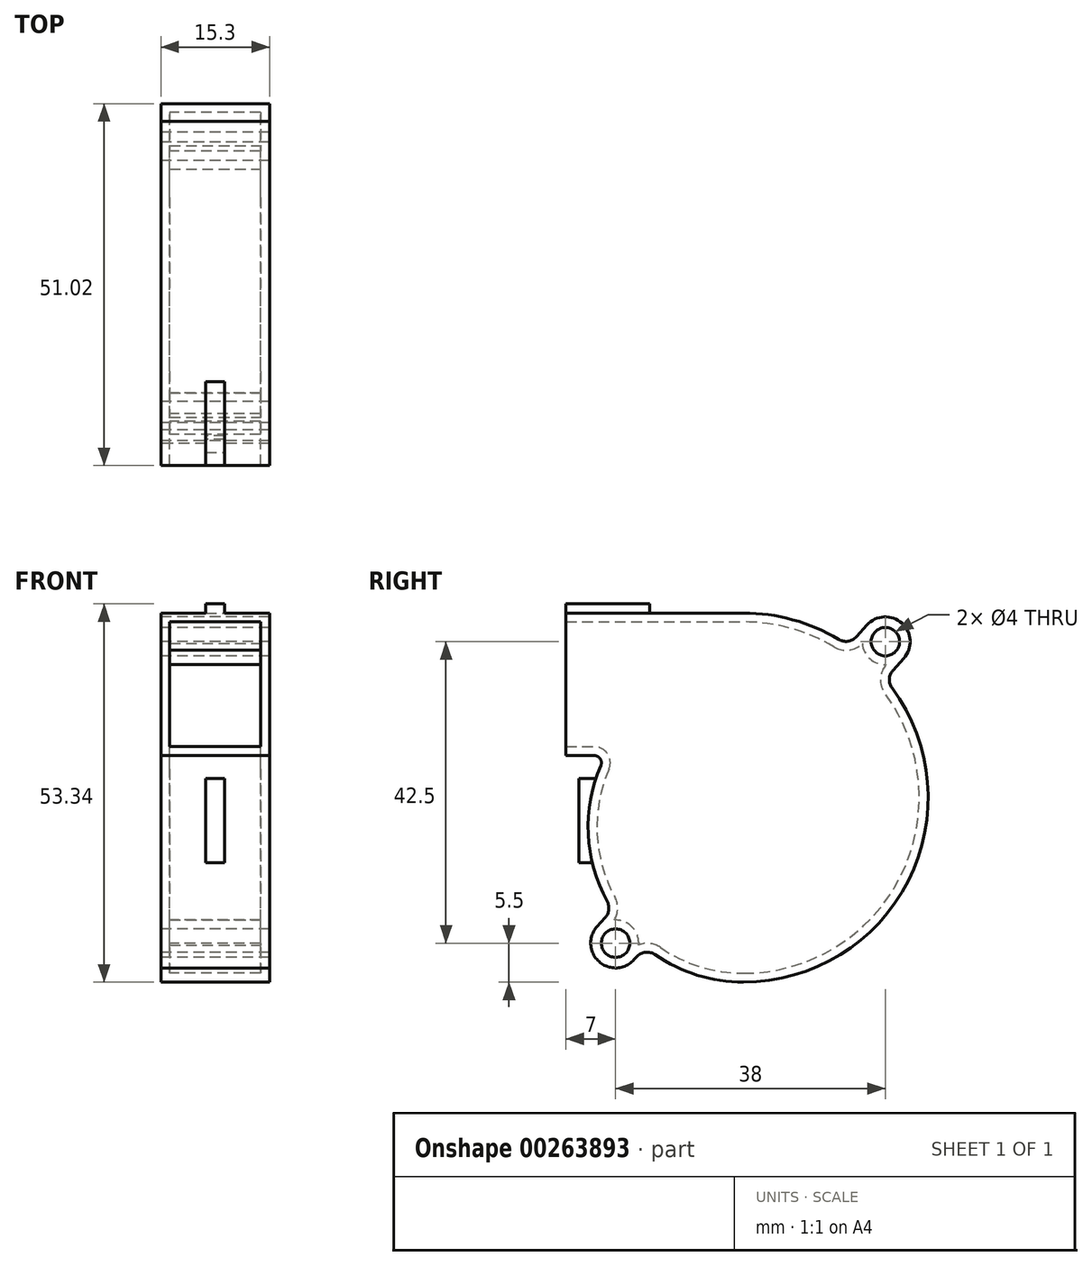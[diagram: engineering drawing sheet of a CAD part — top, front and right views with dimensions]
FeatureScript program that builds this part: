
annotation { "Feature Type Name" : "Feature", "Feature Type Description" : "" }
export const myFeature = defineFeature(function(context is Context, id is Id, definition is map)
    precondition{}
    {
        {
            var Q0;
            Q0=qCreatedBy(makeId("Right.planeOp"),FACE);
            var sketch = newSketch(context, id + "F0", { "sketchPlane" : qUnion([Q0])});
            skCircle(sketch, "E0", {"center": v(0, 0) * mm, "radius": 12 * mm});
            skCircle(sketch, "E1", {"center": v(20, 23) * mm, "radius": 2 * mm});
            skCircle(sketch, "E2", {"center": v(-18, -19.5) * mm, "radius": 2 * mm});
            skLineSegment(sketch, "E3", {"start": v(-25, 27.04) * mm, "end": v(-25, 6.94) * mm});
            skLineSegment(sketch, "E4", {"start": v(26, 45.4) * mm, "end": v(26, -37.85) * mm, "construction": true});
            skCircle(sketch, "E5", {"center": v(0, 0) * mm, "radius": 16 * mm});
            skLineSegment(sketch, "E6", {"start": v(-25, 27.04) * mm, "end": v(65.28, 27.04) * mm, "construction": true});
            skLineSegment(sketch, "E7", {"start": v(-25, 27.04) * mm, "end": v(0, 27.04) * mm});
            skArc(sketch, "E8", {"start": v(22.6, 20.66) * mm, "mid": v(22.34, 25.6) * mm, "end": v(17.4, 25.34) * mm});
            skArc(sketch, "E9", {"start": v(-20.6, -17.16) * mm, "mid": v(-20.34, -22.1) * mm, "end": v(-15.4, -21.84) * mm});
            skArc(sketch, "E10", {"start": v(26, 0) * mm, "mid": v(24.88, 8.65) * mm, "end": v(20.95, 16.45) * mm});
            skArc(sketch, "E11", {"start": v(0, -25) * mm, "mid": v(18.03, -17.74) * mm, "end": v(26, 0) * mm});
            skArc(sketch, "E12", {"start": v(-20.08, 5.54) * mm, "mid": v(-21.85, -4.13) * mm, "end": v(-19.2, -13.6) * mm});
            skLineSegment(sketch, "E13", {"start": v(-25, 6.94) * mm, "end": v(-21, 6.94) * mm});
            skPoint(sketch, "E14.visualSharp", {"position": v(-19.42, 6.94) * mm});
            skArc(sketch, "E14.filletArc", {"start": v(-20.08, 5.54) * mm, "mid": v(-20.16, 6.49) * mm, "end": v(-21, 6.94) * mm});
            skLineSegment(sketch, "E15", {"start": v(-20.6, -17.16) * mm, "end": v(-19.47, -15.9) * mm});
            skLineSegment(sketch, "E16", {"start": v(-15.4, -21.84) * mm, "end": v(-15.04, -21.44) * mm});
            skLineSegment(sketch, "E17", {"start": v(17.4, 25.34) * mm, "end": v(15.92, 23.7) * mm});
            skLineSegment(sketch, "E18", {"start": v(22.6, 20.66) * mm, "end": v(21.08, 18.97) * mm});
            skArc(sketch, "E19.trimOffspring", {"start": v(-12.42, -21.13) * mm, "mid": v(-6.5, -24.01) * mm, "end": v(0, -25) * mm});
            skArc(sketch, "E20.trimOffspring", {"start": v(13.4, 23.32) * mm, "mid": v(6.95, 26.1) * mm, "end": v(0, 27.04) * mm});
            skPoint(sketch, "E21.visualSharp", {"position": v(14.78, 22.44) * mm});
            skArc(sketch, "E21.filletArc", {"start": v(13.4, 23.32) * mm, "mid": v(14.73, 23.06) * mm, "end": v(15.92, 23.7) * mm});
            skPoint(sketch, "E22.visualSharp", {"position": v(19.95, 17.72) * mm});
            skArc(sketch, "E22.filletArc", {"start": v(21.08, 18.97) * mm, "mid": v(20.57, 17.73) * mm, "end": v(20.95, 16.45) * mm});
            skPoint(sketch, "E23.visualSharp", {"position": v(-18.49, -14.81) * mm});
            skArc(sketch, "E23.filletArc", {"start": v(-19.47, -15.9) * mm, "mid": v(-18.97, -14.8) * mm, "end": v(-19.2, -13.6) * mm});
            skPoint(sketch, "E24.visualSharp", {"position": v(-13.82, -20.08) * mm});
            skArc(sketch, "E24.filletArc", {"start": v(-12.42, -21.13) * mm, "mid": v(-13.79, -20.8) * mm, "end": v(-15.04, -21.44) * mm});
            skSolve(sketch);
        }
        {
            var Q0;
            Q0=makeQuery(id+"F0.imprint","IMPRINT",FACE,{"disambiguationData":[TD([[makeQuery(id+"F0.imprint","IMPRINT",EDGE,{"derivedFrom":sQuery(id+"F0.wireOp",EDGE,"E1")}),-1.0]])]});
            var Q1;
            Q1=makeQuery(id+"F0.imprint","IMPRINT",FACE,{"disambiguationData":[TD([[makeQuery(id+"F0.imprint","IMPRINT",EDGE,{"derivedFrom":sQuery(id+"F0.wireOp",EDGE,"E0")}),-1.0]])]});
            var Q2;
            Q2=makeQuery(id+"F0.imprint","IMPRINT",FACE,{"disambiguationData":[TD([[makeQuery(id+"F0.imprint","IMPRINT",EDGE,{"derivedFrom":sQuery(id+"F0.wireOp",EDGE,"E0")}),1.0]])]});
            extrude(context, id + "F1", {"entities" : qUnion([Q0, Q1, Q2]), "endBound" : BoundingType.SYMMETRIC, "depth" : (15 + .3) * mm});
        }
        {
            var Q0;
            Q0=makeQuery(id+"F1.opExtrude","SWEPT_FACE",FACE,{"disambiguationData":[OSD([sQuery(id+"F0.wireOp",EDGE,"E3")])]});
            shell(context, id + "F2", {"entities" : qUnion([Q0]), "thickness" : 1.25 * mm});
        }
        {
            var Q0;
            Q0=makeQuery(id+"F1.opExtrude","SWEPT_FACE",FACE,{"disambiguationData":[OSD([sQuery(id+"F0.wireOp",EDGE,"E7")])]});
            var sketch = newSketch(context, id + "F3", { "sketchPlane" : qUnion([Q0])});
            skLineSegment(sketch, "E25", {"start": v(0, -13.17) * mm, "end": v(0, -25) * mm, "construction": true});
            skPoint(sketch, "E26", {"position": v(0, -19.08) * mm});
            skLineSegment(sketch, "E27.bottom", {"start": v(-1.31, -25) * mm, "end": v(1.32, -25) * mm});
            skLineSegment(sketch, "E27.top", {"start": v(-1.31, -13.17) * mm, "end": v(1.32, -13.17) * mm});
            skLineSegment(sketch, "E27.left", {"start": v(-1.31, -25) * mm, "end": v(-1.31, -13.17) * mm});
            skLineSegment(sketch, "E27.right", {"start": v(1.32, -25) * mm, "end": v(1.32, -13.17) * mm});
            skSolve(sketch);
        }
        {
            var Q0;
            Q0=makeQuery(id+"F3.imprint","IMPRINT",FACE,{"disambiguationData":[TD([[makeQuery(id+"F3.imprint","IMPRINT",EDGE,{"derivedFrom":sQuery(id+"F3.wireOp",EDGE,"E27.bottom")}),-1.0]])]});
            extrude(context, id + "F4", {"entities" : qUnion([Q0]), "operationType" : NewBodyOperationType.ADD, "depth" : 1.3 * mm});
        }
        {
            var Q0;
            Q0=makeQuery(id+"F1.opExtrude","CAP_EDGE",EDGE,{"disambiguationData":[OSD([sQuery(id+"F0.wireOp",EDGE,"E12")])],"isStart":false});
            cPoint(context, id + "F5", {"entities" : qUnion([Q0]), "parameter" : 0.5});
        }
        {
            var Q0;
            Q0=qCreatedBy(id+"F5",VERTEX);
            var Q1;
            Q1=makeQuery(id+"F4.boolean.opBoolean","MERGE",FACE,{"derivedFrom":[makeQuery(id+"F1.opExtrude","SWEPT_FACE",FACE,{"disambiguationData":[OSD([sQuery(id+"F0.wireOp",EDGE,"E3")])]}),makeQuery(id+"F4.opExtrude","SWEPT_FACE",FACE,{"disambiguationData":[OSD([sQuery(id+"F3.wireOp",EDGE,"E27.bottom")])]})]});
            cPlane(context, id + "F6", {"entities" : qUnion([Q0, Q1]), "cplaneType" : CPlaneType.PLANE_POINT, "offset" : 25 * mm, "width" : 150 * mm, "height" : 150 * mm});
        }
        {
            var Q0;
            Q0=qCreatedBy(id+"F6.planeOp",FACE);
            var sketch = newSketch(context, id + "F7", { "sketchPlane" : qUnion([Q0])});
            skLineSegment(sketch, "E28", {"start": v(0, 3.69) * mm, "end": v(0, -8.14) * mm, "construction": true});
            skPoint(sketch, "E29", {"position": v(0, -2.23) * mm});
            skLineSegment(sketch, "E30.bottom", {"start": v(-1.31, -8.14) * mm, "end": v(1.32, -8.14) * mm});
            skLineSegment(sketch, "E30.top", {"start": v(-1.32, 3.69) * mm, "end": v(1.31, 3.69) * mm});
            skLineSegment(sketch, "E30.left", {"start": v(-1.31, -8.14) * mm, "end": v(-1.32, 3.69) * mm});
            skLineSegment(sketch, "E30.right", {"start": v(1.32, -8.14) * mm, "end": v(1.31, 3.69) * mm});
            skSolve(sketch);
        }
        {
            var Q0;
            Q0=qSketchRegion(id+"F7",true);
            extrude(context, id + "F8", {"entities" : qUnion([Q0]), "operationType" : NewBodyOperationType.ADD, "depth" : 1.3 * mm, "hasSecondDirection" : true, "secondDirectionBound" : SecondDirectionBoundingType.UP_TO_NEXT, "secondDirectionOppositeDirection" : true, "secondDirectionDepth" : 25 * mm});
        }
    });
